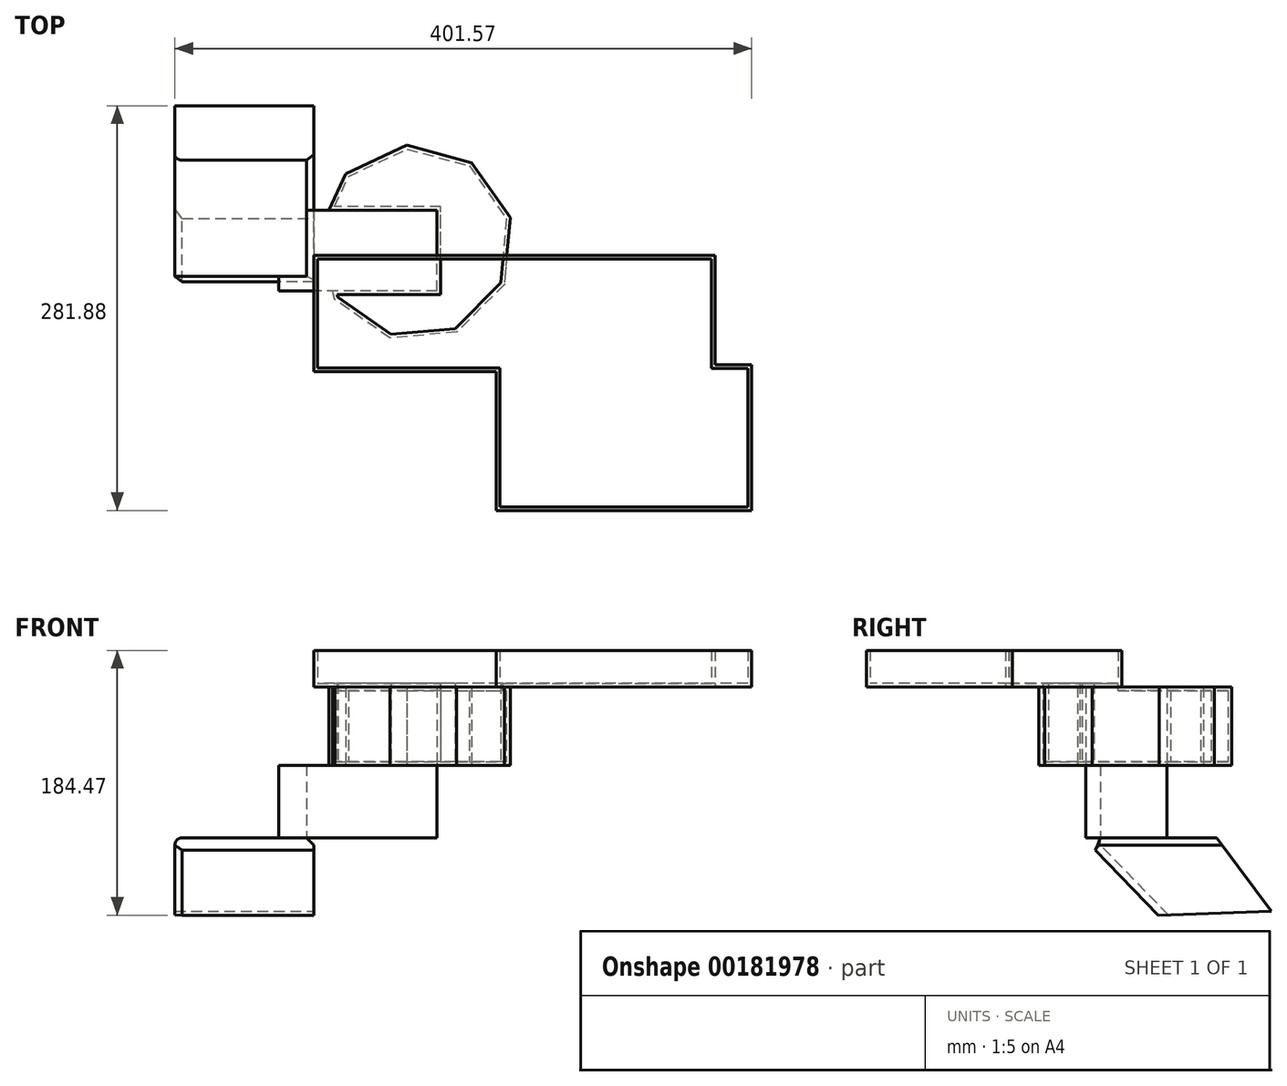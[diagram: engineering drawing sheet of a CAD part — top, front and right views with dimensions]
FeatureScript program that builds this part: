
annotation { "Feature Type Name" : "Feature", "Feature Type Description" : "" }
export const myFeature = defineFeature(function(context is Context, id is Id, definition is map)
    precondition{}
    {
        {
            var Q0;
            Q0=qCreatedBy(makeId("Right.planeOp"),FACE);
            var sketch = newSketch(context, id + "F0", { "sketchPlane" : qUnion([Q0])});
            skLineSegment(sketch, "E0", {"start": v(62.2, -26.5) * mm, "end": v(24.28, 24.67) * mm});
            skLineSegment(sketch, "E1", {"start": v(24.28, 24.67) * mm, "end": v(-68.67, 24.67) * mm});
            skLineSegment(sketch, "E2", {"start": v(-68.67, 24.67) * mm, "end": v(-16.42, -29.25) * mm});
            skLineSegment(sketch, "E3", {"start": v(-16.42, -29.25) * mm, "end": v(62.2, -26.5) * mm});
            skSolve(sketch);
        }
        {
            var Q0;
            Q0=makeQuery(id+"F0.imprint","IMPRINT",FACE,{"disambiguationData":[TD([[makeQuery(id+"F0.imprint","IMPRINT",EDGE,{"derivedFrom":sQuery(id+"F0.wireOp",EDGE,"E0")}),1.0]])]});
            extrude(context, id + "F1", {"entities" : qUnion([Q0]), "oppositeDirection" : true, "depth" : 96.77 * mm});
        }
        {
            var Q0;
            Q0=makeQuery(id+"F1.opExtrude","CAP_EDGE",EDGE,{"disambiguationData":[OSD([sQuery(id+"F0.wireOp",EDGE,"E1")])],"isStart":false});
            fillet(context, id + "F2", {"entities" : qUnion([Q0]), "radius" : 5.08 * mm, "tangentPropagation" : true, "allowEdgeOverflow" : false});
        }
        {
            var Q0;
            Q0=makeQuery(id+"F1.opExtrude","CAP_EDGE",EDGE,{"disambiguationData":[OSD([sQuery(id+"F0.wireOp",EDGE,"E1")])],"isStart":true});
            chamfer(context, id + "F3", {"entities" : qUnion([Q0]), "width" : 5.08 * mm, "tangentPropagation" : true});
        }
        {
            var Q0;
            Q0=makeQuery(id+"F1.opExtrude","SWEPT_EDGE",EDGE,{"disambiguationData":[OSD([sQuery(id+"F0.wireOp",EDGE,"E1"),sQuery(id+"F0.wireOp",EDGE,"E2")])]});
            chamfer(context, id + "F4", {"entities" : qUnion([Q0]), "width" : 5.08 * mm, "tangentPropagation" : true});
        }
        {
            var Q0;
            Q0=makeQuery(id+"F1.opExtrude","SWEPT_FACE",FACE,{"disambiguationData":[OSD([sQuery(id+"F0.wireOp",EDGE,"E1")])]});
            var sketch = newSketch(context, id + "F5", { "sketchPlane" : qUnion([Q0])});
            skLineSegment(sketch, "E4.bottom", {"start": v(85.81, -66.88) * mm, "end": v(-24.43, -66.88) * mm});
            skLineSegment(sketch, "E4.top", {"start": v(85.81, -10.57) * mm, "end": v(-24.43, -10.57) * mm});
            skLineSegment(sketch, "E4.left", {"start": v(85.81, -66.88) * mm, "end": v(85.81, -10.57) * mm});
            skLineSegment(sketch, "E4.right", {"start": v(-24.43, -66.88) * mm, "end": v(-24.43, -10.57) * mm});
            skSolve(sketch);
        }
        {
            var Q0;
            {var subQ1=sQuery(id+"F5.wireOp",EDGE,"E4.bottom");Q0=makeQuery(id+"F5.imprint","IMPRINT",FACE,{"disambiguationData":[TD([[makeQuery(id+"F5.imprint","IMPRINT",EDGE,{"derivedFrom":subQ1}),-1.0]])]});}
            extrude(context, id + "F6", {"entities" : qUnion([Q0]), "depth" : 50.55 * mm});
        }
        {
            var Q0;
            Q0=makeQuery(id+"F6.opExtrude","CAP_FACE",FACE,{"disambiguationData":[OSD([sQuery(id+"F0.wireOp",EDGE,"E1"),sQuery(id+"F0.wireOp",EDGE,"E2"),sQuery(id+"F5.wireOp",EDGE,"E4.bottom"),sQuery(id+"F5.wireOp",EDGE,"E4.top"),sQuery(id+"F5.wireOp",EDGE,"E4.left"),sQuery(id+"F5.wireOp",EDGE,"E4.right")])],"isStart":false});
            var sketch = newSketch(context, id + "F7", { "sketchPlane" : qUnion([Q0])});
            skCircle(sketch, "E5.cCircle", {"center": v(70.63, -33.47) * mm, "radius": 64.29 * mm, "construction": true});
            skLineSegment(sketch, "E5.0", {"start": v(64.67, 34.68) * mm, "end": v(109.87, 22.57) * mm});
            skLineSegment(sketch, "E5.1", {"start": v(109.87, 22.57) * mm, "end": v(136.71, -15.77) * mm});
            skLineSegment(sketch, "E5.2", {"start": v(136.71, -15.77) * mm, "end": v(132.63, -62.39) * mm});
            skLineSegment(sketch, "E5.3", {"start": v(132.63, -62.39) * mm, "end": v(99.54, -95.48) * mm});
            skLineSegment(sketch, "E5.4", {"start": v(99.54, -95.48) * mm, "end": v(52.92, -99.56) * mm});
            skLineSegment(sketch, "E5.5", {"start": v(52.92, -99.56) * mm, "end": v(14.6, -72.71) * mm});
            skLineSegment(sketch, "E5.6", {"start": v(14.6, -72.71) * mm, "end": v(2.48, -27.51) * mm});
            skLineSegment(sketch, "E5.7", {"start": v(2.48, -27.51) * mm, "end": v(22.26, 14.9) * mm});
            skLineSegment(sketch, "E5.8", {"start": v(22.26, 14.9) * mm, "end": v(64.67, 34.68) * mm});
            skPoint(sketch, "E5.0.midPoint", {"position": v(87.27, 28.62) * mm});
            skSolve(sketch);
        }
        {
            var Q0;
            Q0=makeQuery(id+"F7.imprint","IMPRINT",FACE,{"disambiguationData":[TD([[makeQuery(id+"F7.imprint","IMPRINT",EDGE,{"derivedFrom":sQuery(id+"F7.wireOp",EDGE,"E5.0")}),-1.0]])]});
            extrude(context, id + "F8", {"entities" : qUnion([Q0]), "depth" : 54.6 * mm});
        }
        {
            var Q0;
            Q0=makeQuery(id+"F8.opExtrude","CAP_FACE",FACE,{"disambiguationData":[OSD([sQuery(id+"F5.wireOp",EDGE,"E4.bottom"),sQuery(id+"F5.wireOp",EDGE,"E4.top"),sQuery(id+"F5.wireOp",EDGE,"E4.left"),sQuery(id+"F7.wireOp",EDGE,"E5.0"),sQuery(id+"F7.wireOp",EDGE,"E5.1"),sQuery(id+"F7.wireOp",EDGE,"E5.2"),sQuery(id+"F7.wireOp",EDGE,"E5.3"),sQuery(id+"F7.wireOp",EDGE,"E5.4"),sQuery(id+"F7.wireOp",EDGE,"E5.5"),sQuery(id+"F7.wireOp",EDGE,"E5.6"),sQuery(id+"F7.wireOp",EDGE,"E5.7"),sQuery(id+"F7.wireOp",EDGE,"E5.8")])],"isStart":false});
            var sketch = newSketch(context, id + "F9", { "sketchPlane" : qUnion([Q0])});
            skLineSegment(sketch, "E6.bottom", {"start": v(304.8, -118.1) * mm, "end": v(279.4, -118.1) * mm});
            skLineSegment(sketch, "E6.top", {"start": v(304.8, -219.7) * mm, "end": v(127, -219.7) * mm});
            skLineSegment(sketch, "E6.left", {"start": v(304.8, -118.1) * mm, "end": v(304.8, -219.7) * mm});
            skLineSegment(sketch, "E6.right", {"start": v(127, -122.92) * mm, "end": v(127, -219.7) * mm});
            skLineSegment(sketch, "E7", {"start": v(127, -122.92) * mm, "end": v(0, -122.92) * mm});
            skLineSegment(sketch, "E8", {"start": v(0, -122.92) * mm, "end": v(0, -41.9) * mm});
            skLineSegment(sketch, "E9", {"start": v(0, -41.9) * mm, "end": v(279.4, -41.9) * mm});
            skLineSegment(sketch, "E10", {"start": v(279.4, -41.9) * mm, "end": v(279.4, -118.1) * mm});
            skSolve(sketch);
        }
        {
            var Q0;
            Q0=makeQuery(id+"F9.imprint","IMPRINT",FACE,{"disambiguationData":[TD([[makeQuery(id+"F9.imprint","IMPRINT",EDGE,{"derivedFrom":sQuery(id+"F9.wireOp",EDGE,"E6.bottom")}),1.0]])]});
            var Q1;
            {var subQ4=makeQuery(id+"F8.opExtrude","CAP_EDGE",EDGE,{"disambiguationData":[OSD([sQuery(id+"F7.wireOp",EDGE,"E5.3")])],"isStart":false});Q1=makeQuery(id+"F9.imprint","IMPRINT",FACE,{"disambiguationData":[TD([[makeQuery(id+"F9.imprint","IMPRINT",EDGE,{"derivedFrom":subQ4}),-1.0]])]});}
            extrude(context, id + "F10", {"entities" : qUnion([Q0, Q1]), "operationType" : NewBodyOperationType.ADD, "depth" : 25.4 * mm});
        }
        {
            var Q0;
            Q0=makeQuery(id+"F10.opExtrude","CAP_FACE",FACE,{"disambiguationData":[OSD([sQuery(id+"F9.wireOp",EDGE,"E6.bottom"),sQuery(id+"F9.wireOp",EDGE,"E6.top"),sQuery(id+"F9.wireOp",EDGE,"E6.left"),sQuery(id+"F9.wireOp",EDGE,"E6.right"),sQuery(id+"F9.wireOp",EDGE,"E7"),sQuery(id+"F9.wireOp",EDGE,"E8"),sQuery(id+"F9.wireOp",EDGE,"E9"),sQuery(id+"F9.wireOp",EDGE,"E10")])],"isStart":false});
            shell(context, id + "F11", {"entities" : qUnion([Q0]), "thickness" : 2.54 * mm});
        }
    });
